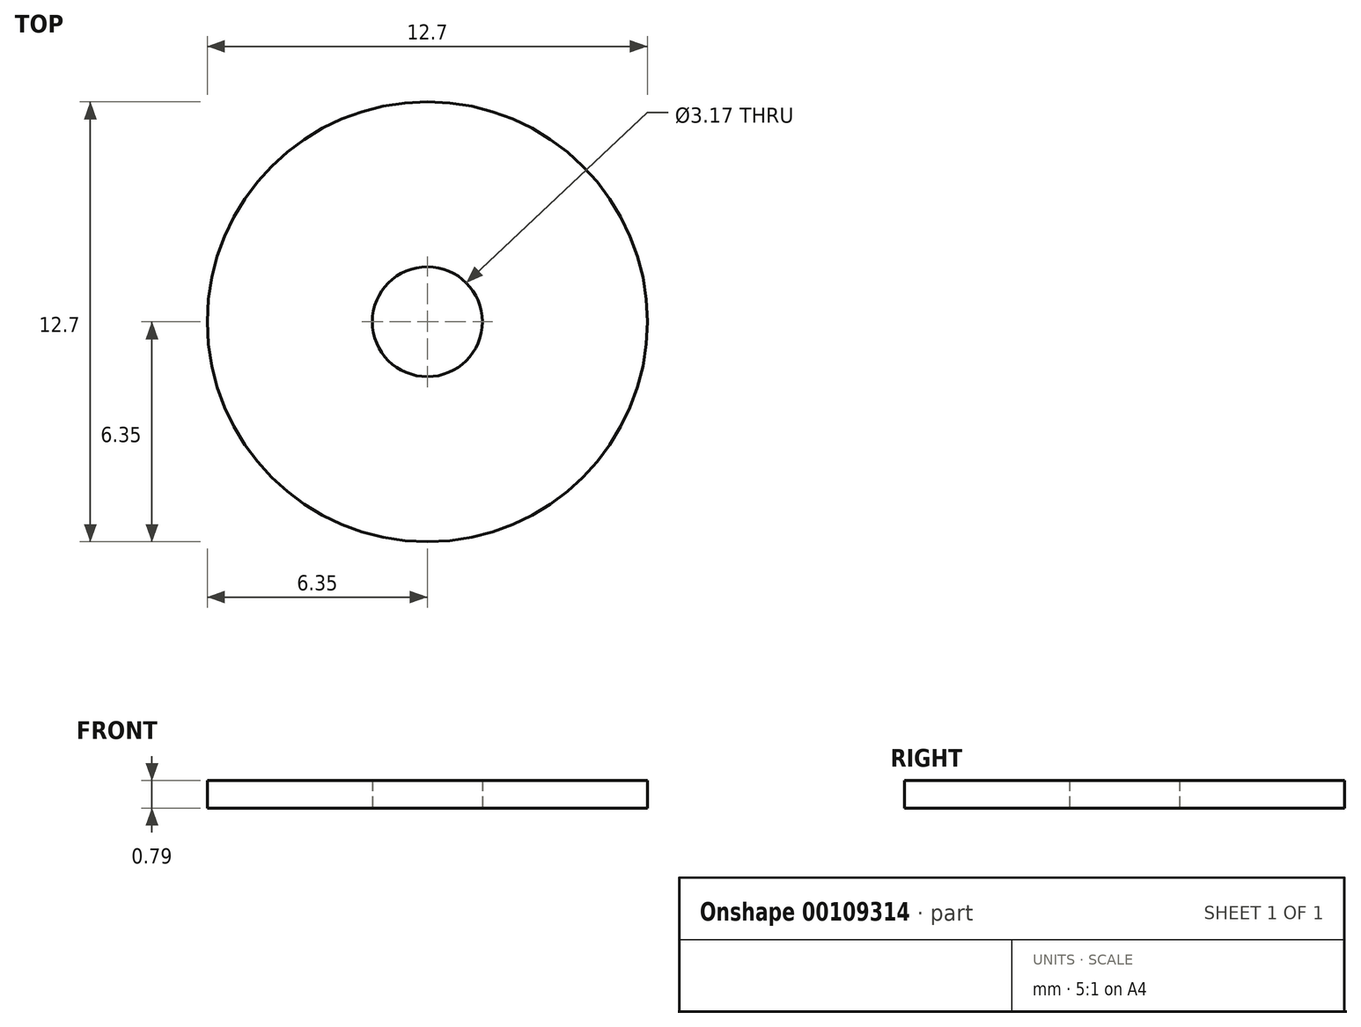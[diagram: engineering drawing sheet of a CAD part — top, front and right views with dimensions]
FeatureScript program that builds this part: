
annotation { "Feature Type Name" : "Feature", "Feature Type Description" : "" }
export const myFeature = defineFeature(function(context is Context, id is Id, definition is map)
    precondition{}
    {
        {
            var Q0;
            Q0=qCreatedBy(makeId("Top.planeOp"),FACE);
            var sketch = newSketch(context, id + "F0", { "sketchPlane" : qUnion([Q0])});
            skCircle(sketch, "E0", {"center": v(0, 0) * mm, "radius": 6.35 * mm});
            skCircle(sketch, "E1", {"center": v(0, 0) * mm, "radius": 1.59 * mm});
            skSolve(sketch);
        }
        {
            var Q0;
            Q0=makeQuery(id+"F0.imprint","IMPRINT",FACE,{"disambiguationData":[TD([[makeQuery(id+"F0.imprint","IMPRINT",EDGE,{"derivedFrom":sQuery(id+"F0.wireOp",EDGE,"E0")}),1.0]])]});
            extrude(context, id + "F1", {"entities" : qUnion([Q0]), "depth" : 0.8 * mm});
        }
    });
